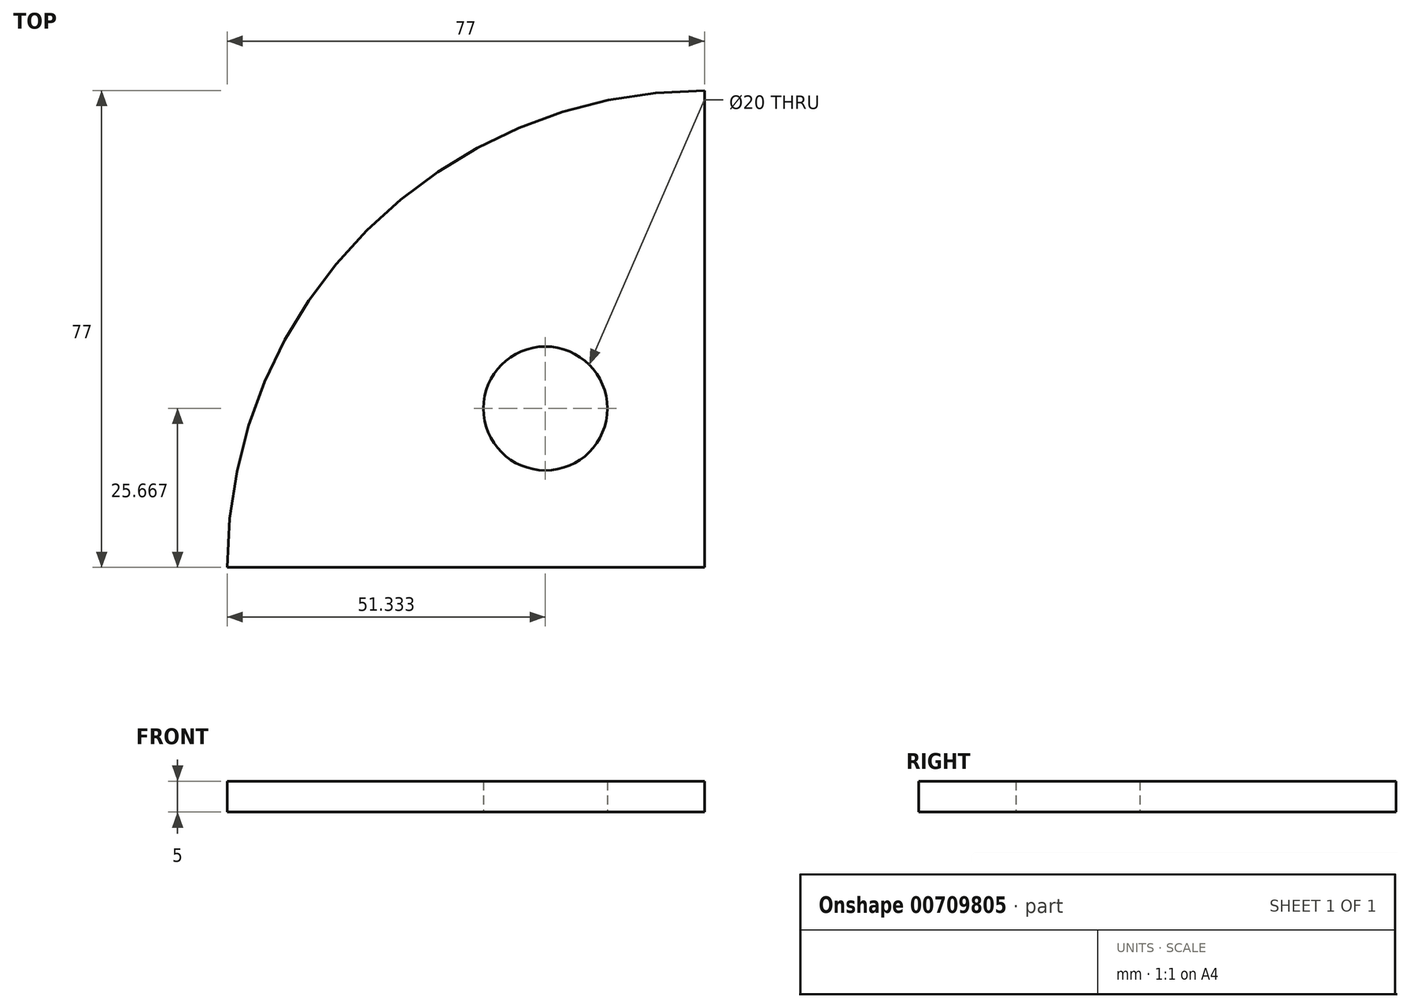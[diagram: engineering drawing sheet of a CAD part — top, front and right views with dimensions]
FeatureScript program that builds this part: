
annotation { "Feature Type Name" : "Feature", "Feature Type Description" : "" }
export const myFeature = defineFeature(function(context is Context, id is Id, definition is map)
    precondition{}
    {
        {
            var Q0;
            Q0=qCreatedBy(makeId("Top.planeOp"),FACE);
            var sketch = newSketch(context, id + "F0", { "sketchPlane" : qUnion([Q0])});
            skArc(sketch, "E0", {"start": v(0, 77) * mm, "mid": v(-54.45, 54.45) * mm, "end": v(-77, 0) * mm});
            skLineSegment(sketch, "E1", {"start": v(0, 0) * mm, "end": v(0, 77) * mm});
            skLineSegment(sketch, "E2", {"start": v(0, 0) * mm, "end": v(-77, 0) * mm});
            skLineSegment(sketch, "E3", {"start": v(-38.5, 0) * mm, "end": v(0, 77) * mm, "construction": true});
            skLineSegment(sketch, "E4", {"start": v(0, 38.5) * mm, "end": v(-25.67, 25.67) * mm, "construction": true});
            skLineSegment(sketch, "E5", {"start": v(-25.67, 25.67) * mm, "end": v(-77, 0) * mm, "construction": true});
            skCircle(sketch, "E6", {"center": v(-25.67, 25.67) * mm, "radius": 10 * mm});
            skSolve(sketch);
        }
        {
            var Q0;
            Q0=makeQuery(id+"F0.imprint","IMPRINT",FACE,{"disambiguationData":[TD([[makeQuery(id+"F0.imprint","IMPRINT",EDGE,{"derivedFrom":sQuery(id+"F0.wireOp",EDGE,"E0")}),1.0]])]});
            extrude(context, id + "F1", {"entities" : qUnion([Q0]), "depth" : 5 * mm, "offsetDistance" : 25 * mm});
        }
    });
